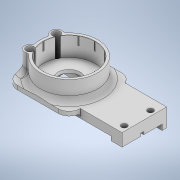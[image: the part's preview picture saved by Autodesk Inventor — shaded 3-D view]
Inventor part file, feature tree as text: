
AUTODESK INVENTOR PART (.ipt)
format: ipt  version: 2022 (Build 260153000, 153)  size: 657,920 bytes
history: native  units: mm
features: extrude x13, sketch x12, fillet x7, other x3, projected_geometry x2, mirror x1, pattern_circular x1
ambient origin geometry x8: Origin, YZ Plane, XZ Plane, XY Plane, X Axis, Y Axis, Z Axis, Center Point
bodies: Body1 (feature_tree)
feature tree (39):
  extrude  "Выдавливание2"  Depth=28.6mm
  sketch  "Эскиз2"
  extrude  "Выдавливание3"  Depth=12.05mm
  extrude  "Выдавливание11"  Depth=31.58mm
  extrude  "Выдавливание12"  Depth=14.05mm
  extrude  "Выдавливание13"  Depth=29.1mm
  extrude  "Выдавливание14"  Depth=75.0mm
  other  "РабПлоскость2"
  mirror  "Зеркальное отражение2"
  extrude  "Выдавливание15"  Depth=3.0mm
  extrude  "Выдавливание18"  Depth=4.0mm TaperAngle=0.0deg
  fillet  "Сопряжение5"  Radius=4.1mm
  extrude  "Выдавливание19"  Depth=19.0mm
  fillet  "Сопряжение6"  Radius=68.0mm
  other  "РабОсь1"
  pattern_circular  "Круговой массив1"  [2 undecoded]
  extrude  "Выдавливание20"  Depth=4.1mm TaperAngle=0.0deg
  extrude  "Выдавливание21"  Depth=22.25mm
  fillet  "Сопряжение8"  Radius=16.0mm
  fillet  "Сопряжение9"  Radius=2.1mm
  other  "РабПлоскость4"
  extrude  "Выдавливание26"  Depth=59.05mm
  fillet  "Сопряжение10"  Radius=28.6mm
  extrude  "Выдавливание27"  Depth=4.475mm
  fillet  "Сопряжение11"  Radius=3.0mm
  fillet  "Сопряжение12"  Radius=4.0mm
  sketch  "Эскиз1"
  sketch  "Эскиз9"
  sketch  "Эскиз10"
  sketch  "Эскиз11"
  sketch  "Эскиз12"
  sketch  "Эскиз13"
  sketch  "Эскиз15"
  sketch  "Эскиз16"
  sketch  "Эскиз17"
  sketch  "Эскиз18"
  sketch  "Эскиз24"
  projected_geometry  "Спроецированная петля1"
  projected_geometry  "Спроецированная петля2"
note: 2 required parameter values undecoded (feature->parameter linkage not recoverable at this tier; creation-order binding heuristic only, values carry confidence <= 0.55)
